# Revit family: Bernhardt_Design-Seating-Benches-Elevation
name_source: partatom
category: Furniture
revit_build: Autodesk Revit 2016 (Build: 20150714_1515(x64)
units: mm (PartAtom-declared; Revit-internal decimal feet)

## family parameters
Always vertical = Yes
Cut with Voids When Loaded = No
OmniClass Number = 23.40.20.00
OmniClass Title = General Furniture and Specialties
Room Calculation Point = No
Shared = No
Work Plane-Based = No

## types (16) — shared parameters
Fabric = <By Category>
LegL_toEdge = 8 5/16"
LegR_toEdge = 7 27/32"
Manufacturer = Bernhardt Design
Model = Elevation
URL = http://www.bernhardtdesign.com

## per-type parameters (varying)
| type | AsymmetricFin | BenchLength | Metal | ThirdFin | Wood |
| Elevation 3801A | Yes | 68" | Aluminum - Bronze Powdercoat | No | Bernhardt - Oak default |
| Elevation 3801AK | Yes | 68" | Aluminum - Matte Black Powdercoat | No | Bernhardt - Oak default |
| Elevation 3802A | Yes | 68" | Aluminum - Bronze Powdercoat | No | Bernhardt - Walnut default |
| Elevation 3802AK | Yes | 68" | Aluminum - Matte Black Powdercoat | No | Bernhardt - Walnut default |
| Elevation 3803A | No | 68" | Aluminum - Bronze Powdercoat | No | Bernhardt - Oak default |
| Elevation 3803AK | No | 68" | Aluminum - Matte Black Powdercoat | No | Bernhardt - Oak default |
| Elevation 3804A | No | 68" | Aluminum - Bronze Powdercoat | No | Bernhardt - Walnut default |
| Elevation 3804AK | No | 68" | Aluminum - Matte Black Powdercoat | No | Bernhardt - Walnut default |
| Elevation 3811A | Yes | 92" | Aluminum - Bronze Powdercoat | No | Bernhardt - Oak default |
| Elevation 3811AK | Yes | 92" | Aluminum - Matte Black Powdercoat | No | Bernhardt - Oak default |
| Elevation 3812A | Yes | 92" | Aluminum - Bronze Powdercoat | No | Bernhardt - Walnut default |
| Elevation 3812AK | Yes | 92" | Aluminum - Matte Black Powdercoat | No | Bernhardt - Walnut default |
| Elevation 3813A | No | 92" | Aluminum - Bronze Powdercoat | Yes | Bernhardt - Oak default |
| Elevation 3813AK | No | 92" | Aluminum - Matte Black Powdercoat | Yes | Bernhardt - Oak default |
| Elevation 3814A | No | 92" | Aluminum - Bronze Powdercoat | Yes | Bernhardt - Walnut default |
| Elevation 3814AK | No | 92" | Aluminum - Matte Black Powdercoat | Yes | Bernhardt - Walnut default |

note: column(s) folded — value = type name in every type: SKU

## geometry (parser evidence)
native form markers: Sweep x3
no freeform markers — native parametric forms only
